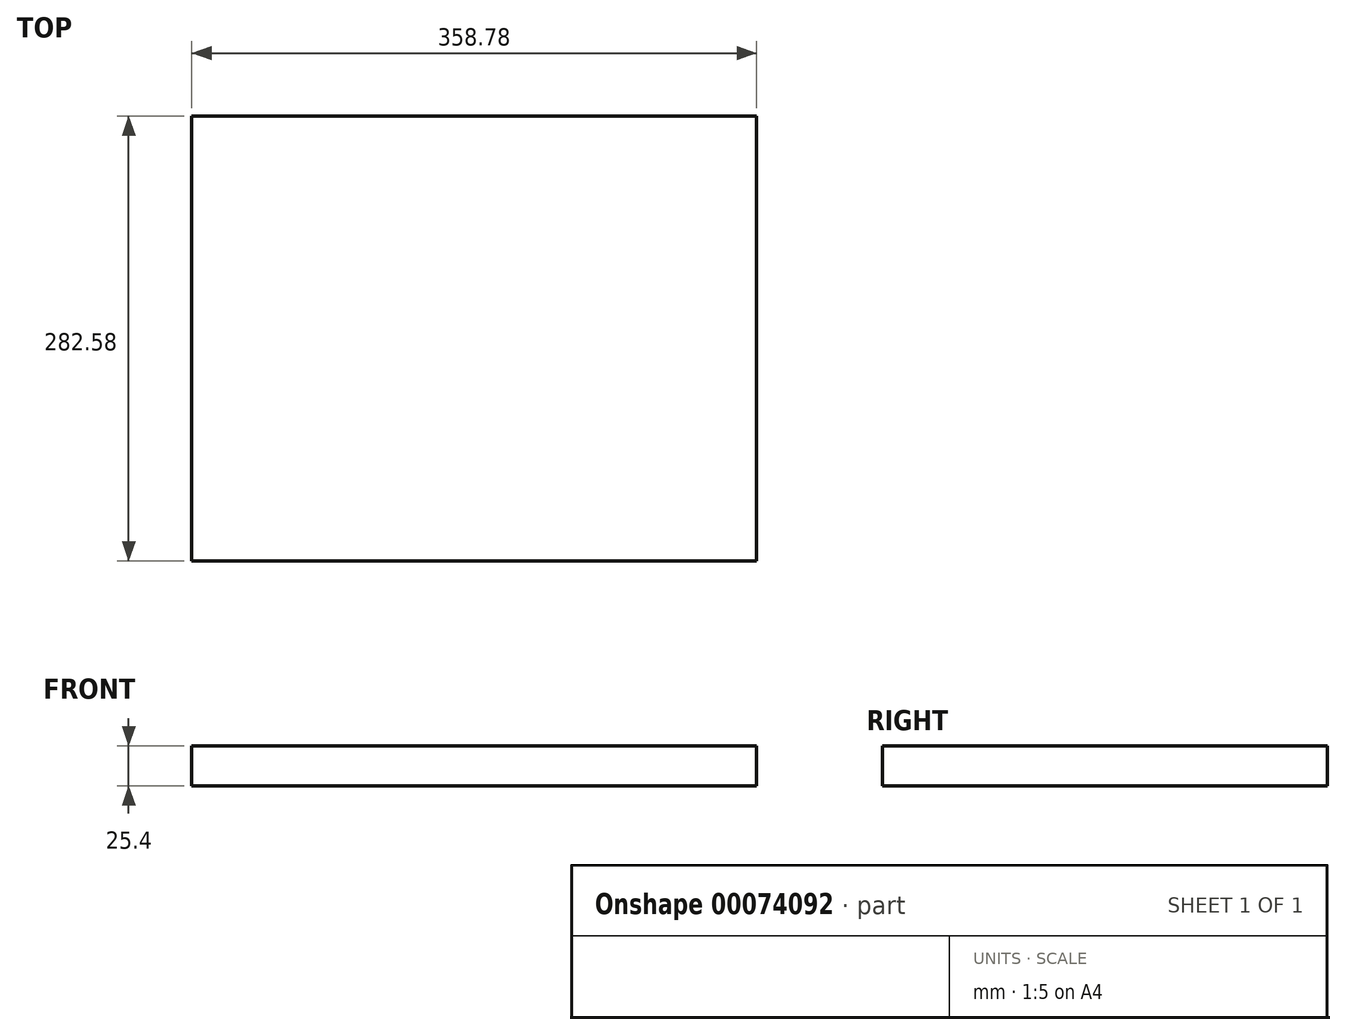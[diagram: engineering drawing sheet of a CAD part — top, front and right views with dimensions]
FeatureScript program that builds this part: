
annotation { "Feature Type Name" : "Feature", "Feature Type Description" : "" }
export const myFeature = defineFeature(function(context is Context, id is Id, definition is map)
    precondition{}
    {
        {
            var Q0;
            Q0=qCreatedBy(makeId("Top.planeOp"),FACE);
            var sketch = newSketch(context, id + "F0", { "sketchPlane" : qUnion([Q0])});
            skLineSegment(sketch, "E0.rect.bottom", {"start": v(179.39, -141.29) * mm, "end": v(-179.39, -141.29) * mm});
            skLineSegment(sketch, "E0.rect.top", {"start": v(179.39, 141.29) * mm, "end": v(-179.39, 141.29) * mm});
            skLineSegment(sketch, "E0.rect.left", {"start": v(179.39, -141.29) * mm, "end": v(179.39, 141.29) * mm});
            skLineSegment(sketch, "E0.rect.right", {"start": v(-179.39, -141.29) * mm, "end": v(-179.39, 141.29) * mm});
            skPoint(sketch, "E0.rect.middle", {"position": v(0, 0) * mm});
            skSolve(sketch);
        }
        {
            var Q0;
            Q0=qSketchRegion(id+"F0",true);
            extrude(context, id + "F1", {"entities" : qUnion([Q0]), "depth" : 25.4 * mm});
        }
    });
